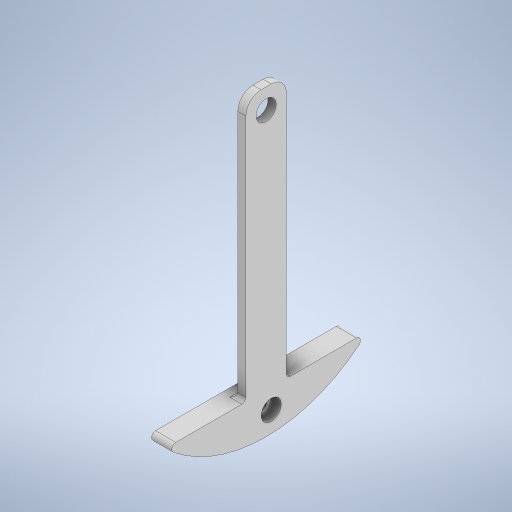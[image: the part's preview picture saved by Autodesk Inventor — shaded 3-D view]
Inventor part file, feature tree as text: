
AUTODESK INVENTOR PART (.ipt)
format: ipt  version: 2023 (Build 270158000, 158)  size: 281,088 bytes
history: native  units: mm
features: sketch x4, fillet x3, extrude x2, hole x2
ambient origin geometry x8: Origin, YZ Plane, XZ Plane, XY Plane, X Axis, Y Axis, Z Axis, Center Point
bodies: Body1 (feature_tree)
feature tree (11):
  extrude  "押し出し3"  Depth=100.0mm
  extrude  "押し出し4"  Depth=20.0mm
  hole  "穴2"  [1 undecoded]
  hole  "穴3"  [1 undecoded]
  fillet  "フィレット1"  Radius=130.0mm
  fillet  "フィレット2"  [1 undecoded]
  fillet  "フィレット3"  [1 undecoded]
  sketch  "スケッチ4"
  sketch  "スケッチ5"
  sketch  "スケッチ6"
  sketch  "スケッチ7"
note: 4 required parameter values undecoded (feature->parameter linkage not recoverable at this tier; creation-order binding heuristic only, values carry confidence <= 0.55)
